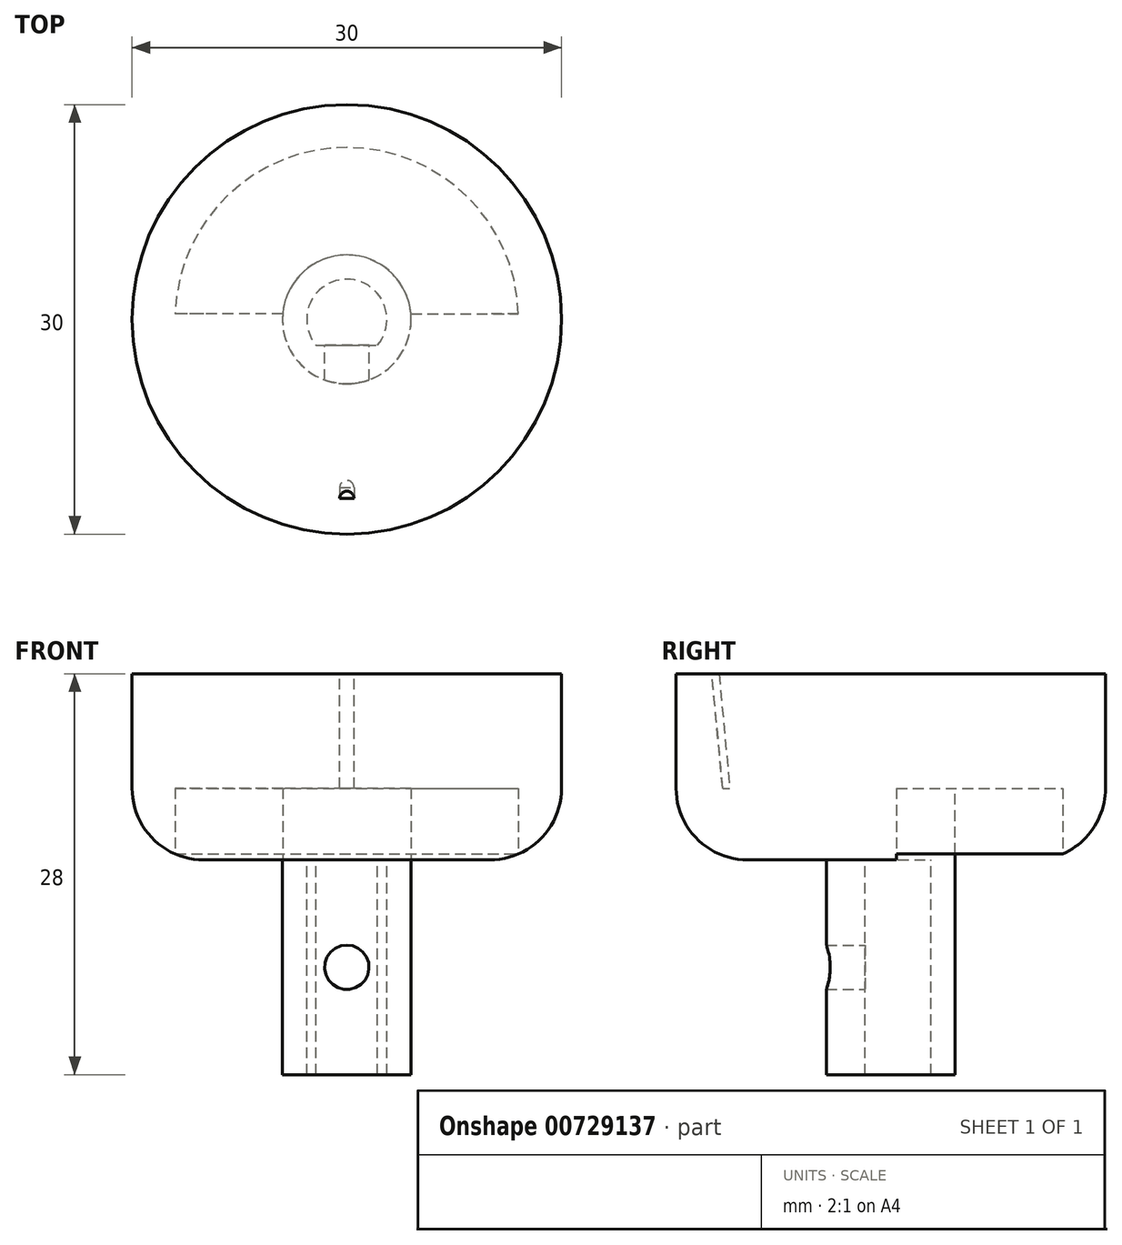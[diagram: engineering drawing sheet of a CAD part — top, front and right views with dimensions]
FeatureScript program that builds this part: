
annotation { "Feature Type Name" : "Feature", "Feature Type Description" : "" }
export const myFeature = defineFeature(function(context is Context, id is Id, definition is map)
    precondition{}
    {
        {
            var Q0;
            Q0=qCreatedBy(makeId("Top.planeOp"),FACE);
            var sketch = newSketch(context, id + "F0", { "sketchPlane" : qUnion([Q0])});
            skLineSegment(sketch, "E0", {"start": v(-2.14, -1.8) * mm, "end": v(2.14, -1.8) * mm});
            skArc(sketch, "E1", {"start": v(-2.14, -1.8) * mm, "mid": v(0, 2.8) * mm, "end": v(2.14, -1.8) * mm});
            skCircle(sketch, "E2", {"center": v(0, 0) * mm, "radius": 15 * mm});
            skCircle(sketch, "E3", {"center": v(0, 0) * mm, "radius": 4.5 * mm});
            skCircle(sketch, "E4", {"center": v(0, 0) * mm, "radius": 12 * mm});
            skSolve(sketch);
        }
        {
            var Q0;
            Q0=makeQuery(id+"F0.imprint","IMPRINT",FACE,{"disambiguationData":[TD([[makeQuery(id+"F0.imprint","IMPRINT",EDGE,{"derivedFrom":sQuery(id+"F0.wireOp",EDGE,"E0")}),-1.0]])]});
            var Q1;
            Q1=sQuery(id+"F0.wireOp",EDGE,"E1");
            var Q2;
            Q2=sQuery(id+"F0.wireOp",EDGE,"E0");
            extrude(context, id + "F1", {"entities" : qUnion([Q0]), "surfaceEntities" : qUnion([Q1, Q2]), "oppositeDirection" : true, "depth" : 15 * mm, "offsetDistance" : 25 * mm});
        }
        {
            var Q0;
            Q0=makeQuery(id+"F0.imprint","IMPRINT",FACE,{"disambiguationData":[TD([[makeQuery(id+"F0.imprint","IMPRINT",EDGE,{"derivedFrom":sQuery(id+"F0.wireOp",EDGE,"E3")}),-1.0]])]});
            var Q1;
            Q1=makeQuery(id+"F0.imprint","IMPRINT",FACE,{"disambiguationData":[TD([[makeQuery(id+"F0.imprint","IMPRINT",EDGE,{"derivedFrom":sQuery(id+"F0.wireOp",EDGE,"E0")}),1.0]])]});
            var Q2;
            Q2=makeQuery(id+"F0.imprint","IMPRINT",FACE,{"disambiguationData":[TD([[makeQuery(id+"F0.imprint","IMPRINT",EDGE,{"derivedFrom":sQuery(id+"F0.wireOp",EDGE,"E0")}),-1.0]])]});
            extrude(context, id + "F2", {"entities" : qUnion([Q0, Q1, Q2]), "operationType" : NewBodyOperationType.ADD, "depth" : 5 * mm, "offsetDistance" : 25 * mm});
        }
        {
            var Q0;
            {var subQ0=sQuery(id+"F0.wireOp",EDGE,"E0");Q0=makeQuery(id+"F2.boolean.opBoolean","MERGE",FACE,{"derivedFrom":[makeQuery(id+"F1.opExtrude","SWEPT_FACE",FACE,{"disambiguationData":[OSD([subQ0])]}),makeQuery(id+"F2.opExtrude","SWEPT_FACE",FACE,{"disambiguationData":[OSD([subQ0])]})]});}
            var sketch = newSketch(context, id + "F3", { "sketchPlane" : qUnion([Q0])});
            skPoint(sketch, "E5", {"position": v(0, -7.5) * mm});
            skSolve(sketch);
        }
        {
            var Q0;
            Q0=sQuery(id+"F3.wireOp",VERTEX,"E5");
            var Q1;
            Q1=makeQuery(id+"F1.opExtrude","SWEPT_BODY",BODY,{"disambiguationData":[OSD([sQuery(id+"F0.wireOp",EDGE,"E0"),sQuery(id+"F0.wireOp",EDGE,"E1"),sQuery(id+"F0.wireOp",EDGE,"E3")])]});
            hole(context, id + "F4", {"style" : HoleStyle.SIMPLE, "endStyle" : HoleEndStyle.THROUGH, "holeDiameter" : 3.1 * mm, "majorDiameter" : 5 * mm, "isTappedThrough" : true, "tappedDepth" : 12 * mm, "tapClearance" : 3, "locations" : qUnion([Q0]), "scope" : qUnion([Q1])});
        }
        {
            var Q0;
            Q0=qCreatedBy(makeId("Right.planeOp"),FACE);
            var sketch = newSketch(context, id + "F5", { "sketchPlane" : qUnion([Q0])});
            skLineSegment(sketch, "E6", {"start": v(11.75, 0) * mm, "end": v(15, 0) * mm});
            skLineSegment(sketch, "E7", {"start": v(15, 13) * mm, "end": v(12.5, 13) * mm});
            skLineSegment(sketch, "E8", {"start": v(15, 13) * mm, "end": v(15, 0) * mm});
            skLineSegment(sketch, "E9", {"start": v(11.75, 0) * mm, "end": v(11.75, 5) * mm});
            skLineSegment(sketch, "E10", {"start": v(11.75, 5) * mm, "end": v(12.5, 13) * mm});
            skLineSegment(sketch, "E11", {"start": v(0, 9.96) * mm, "end": v(0, -1.49) * mm, "construction": true});
            skLineSegment(sketch, "E12", {"start": v(0, 13) * mm, "end": v(12.5, 13) * mm, "construction": true});
            skSolve(sketch);
        }
        {
            var Q0;
            Q0=makeQuery(id+"F5.imprint","IMPRINT",FACE,{"disambiguationData":[TD([[makeQuery(id+"F5.imprint","IMPRINT",EDGE,{"derivedFrom":sQuery(id+"F5.wireOp",EDGE,"E6")}),1.0]])]});
            var Q1;
            Q1=sQuery(id+"F5.wireOp",EDGE,"E11");
            revolve(context, id + "F6", {"operationType" : NewBodyOperationType.ADD, "surfaceOperationType" : NewSurfaceOperationType.NEW, "entities" : qUnion([Q0]), "axis" : qUnion([Q1]), "revolveType" : RevolveType.FULL});
        }
        {
            var Q0;
            Q0=makeQuery(id+"F2.opExtrude","CAP_FACE",FACE,{"disambiguationData":[OSD([sQuery(id+"F0.wireOp",EDGE,"E4")])],"isStart":false});
            var sketch = newSketch(context, id + "F7", { "sketchPlane" : qUnion([Q0])});
            skCircle(sketch, "E13", {"center": v(0, 0) * mm, "radius": 11.75 * mm, "construction": true});
            skLineSegment(sketch, "E14", {"start": v(0.5, 11.74) * mm, "end": v(0.5, 11.74) * mm});
            skArc(sketch, "E15", {"start": v(-0.5, -11.74) * mm, "mid": v(0, -11.25) * mm, "end": v(0.5, -11.74) * mm});
            skSolve(sketch);
        }
        {
            var Q0;
            {var subQ0=sQuery(id+"F0.wireOp",EDGE,"E4");Q0=makeQuery(id+"F6.boolean.opBoolean","MERGE",FACE,{"derivedFrom":[makeQuery(id+"F2.boolean.opBoolean","SPLIT",FACE,{"disambiguationData":[TD([makeQuery(id+"F1.opExtrude","SWEPT_FACE",FACE,{"disambiguationData":[OSD([sQuery(id+"F0.wireOp",EDGE,"E3")])]})])],"derivedFrom":makeQuery(id+"F2.opExtrude","CAP_FACE",FACE,{"disambiguationData":[OSD([subQ0])],"isStart":true})}),makeQuery(id+"F6.opRevolve","SWEPT_FACE",FACE,{"disambiguationData":[OSD([sQuery(id+"F5.wireOp",EDGE,"E6")])]})]});}
            var sketch = newSketch(context, id + "F8", { "sketchPlane" : qUnion([Q0])});
            skCircle(sketch, "E16", {"center": v(0, 0) * mm, "radius": 12 * mm});
            skLineSegment(sketch, "E17", {"start": v(0, 0) * mm, "end": v(-12, 0) * mm, "construction": true});
            skCircle(sketch, "E18", {"center": v(0, 0) * mm, "radius": 4.5 * mm});
            skLineSegment(sketch, "E19", {"start": v(-4.48, -0.4) * mm, "end": v(-12, -0.4) * mm});
            skLineSegment(sketch, "E20", {"start": v(-4.48, 0.4) * mm, "end": v(-12, 0.4) * mm});
            skLineSegment(sketch, "E21", {"start": v(0, 0) * mm, "end": v(12, 0) * mm, "construction": true});
            skLineSegment(sketch, "E22", {"start": v(4.48, -0.4) * mm, "end": v(12, -0.4) * mm});
            skLineSegment(sketch, "E23", {"start": v(4.48, 0.4) * mm, "end": v(12, 0.4) * mm});
            skSolve(sketch);
        }
        {
            var Q0;
            Q0=makeQuery(id+"F6.opRevolve","SWEPT_FACE",FACE,{"disambiguationData":[OSD([sQuery(id+"F5.wireOp",EDGE,"E7")])]});
            var sketch = newSketch(context, id + "F9", { "sketchPlane" : qUnion([Q0])});
            skArc(sketch, "E24", {"start": v(-0.5, -12.5) * mm, "mid": v(0, -12) * mm, "end": v(0.5, -12.5) * mm});
            skSolve(sketch);
        }
        {
            var Q0;
            {var subQ0=sQuery(id+"F8.wireOp",EDGE,"E19");Q0=makeQuery(id+"F8.imprint","IMPRINT",FACE,{"disambiguationData":[TD([[makeQuery(id+"F8.imprint","IMPRINT",EDGE,{"derivedFrom":subQ0}),1.0]])]});}
            extrude(context, id + "F10", {"entities" : qUnion([Q0]), "operationType" : NewBodyOperationType.REMOVE, "oppositeDirection" : true, "depth" : 5 * mm, "offsetDistance" : 25 * mm});
        }
        {
            var Q1;
            {var subQ0=sQuery(id+"F7.wireOp",EDGE,"E15");Q1=makeQuery(id+"F7.imprint","IMPRINT",FACE,{"disambiguationData":[TD([[makeQuery(id+"F7.imprint","IMPRINT",EDGE,{"derivedFrom":subQ0}),-1.0]])]});}
            var Q2;
            {var subQ0=sQuery(id+"F9.wireOp",EDGE,"E24");Q2=makeQuery(id+"F9.imprint","IMPRINT",FACE,{"disambiguationData":[TD([[makeQuery(id+"F9.imprint","IMPRINT",EDGE,{"derivedFrom":subQ0}),-1.0]])]});}
            loft(context, id + "F11", {"operationType" : NewBodyOperationType.ADD, "sheetProfilesArray" : [{ "sheetProfileEntities" : qUnion([Q1]) }, { "sheetProfileEntities" : qUnion([Q2]) }]});
        }
        {
            var Q0;
            Q0=makeQuery(id+"F6.opRevolve","SWEPT_EDGE",EDGE,{"disambiguationData":[OSD([sQuery(id+"F5.wireOp",EDGE,"E6"),sQuery(id+"F5.wireOp",EDGE,"E8")])]});
            fillet(context, id + "F12", {"entities" : qUnion([Q0]), "radius" : 5 * mm, "tangentPropagation" : true, "allowEdgeOverflow" : false});
        }
    });
